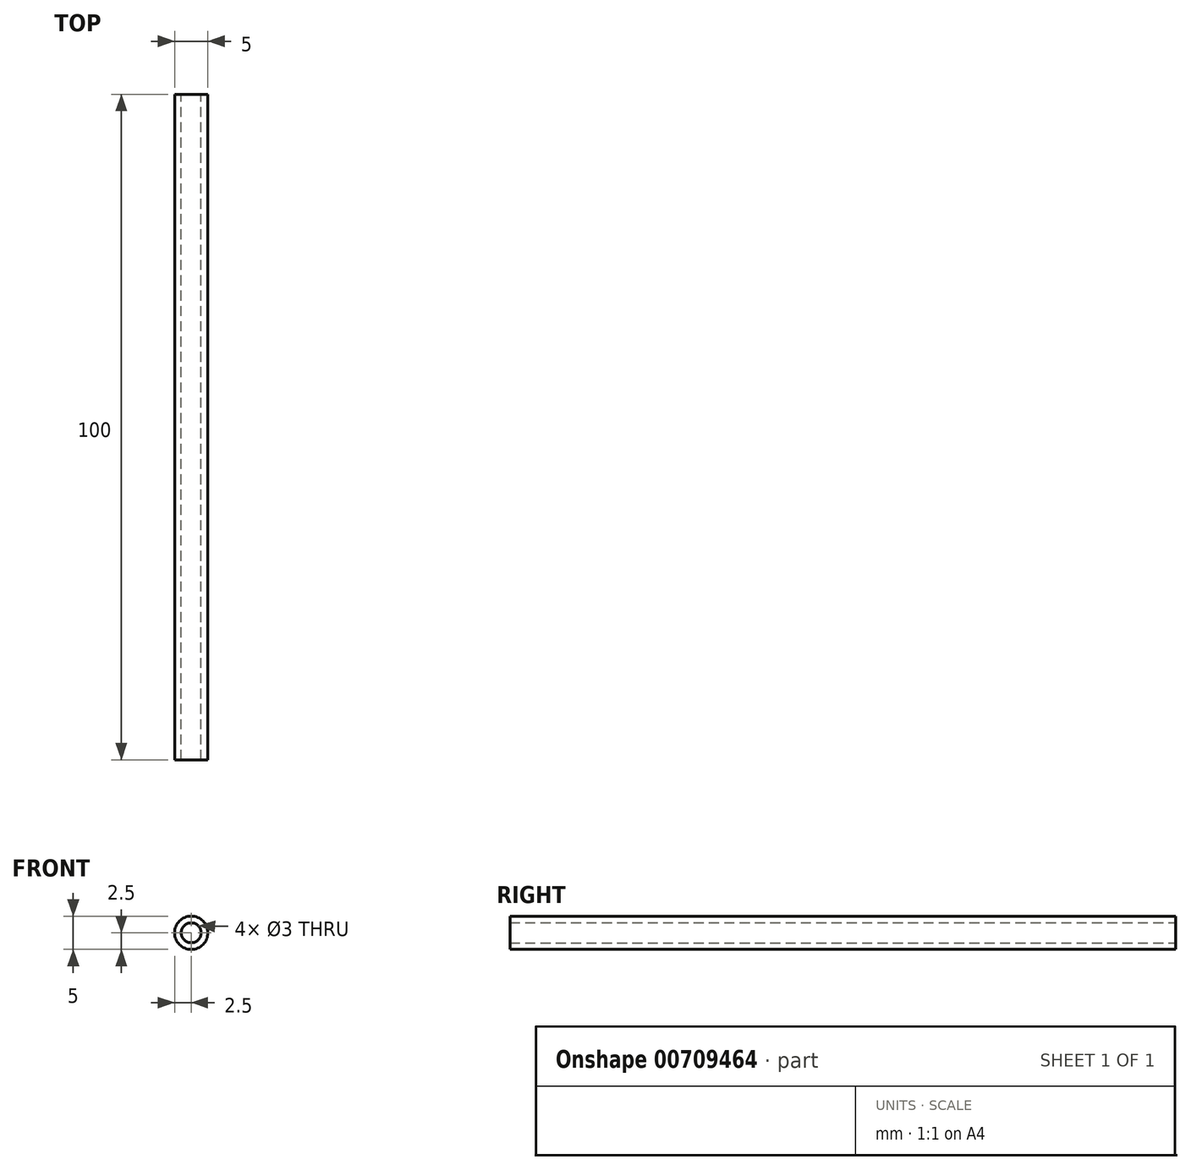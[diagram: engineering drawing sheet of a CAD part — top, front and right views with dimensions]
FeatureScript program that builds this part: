
annotation { "Feature Type Name" : "Feature", "Feature Type Description" : "" }
export const myFeature = defineFeature(function(context is Context, id is Id, definition is map)
    precondition{}
    {
        {
            var Q0;
            Q0=qCreatedBy(makeId("Front.planeOp"),FACE);
            var sketch = newSketch(context, id + "F0", { "sketchPlane" : qUnion([Q0])});
            skCircle(sketch, "E0", {"center": v(0, 0) * mm, "radius": 2.5 * mm});
            skCircle(sketch, "E1", {"center": v(0, 0) * mm, "radius": 1.5 * mm});
            skSolve(sketch);
        }
        {
            var Q0;
            Q0 = qSketchRegion(id + "F0", true);
            extrude(context, id + "F1", {"entities" : qUnion([Q0]), "depth" : 100 * mm, "offsetDistance" : 25 * mm});
        }
    });
